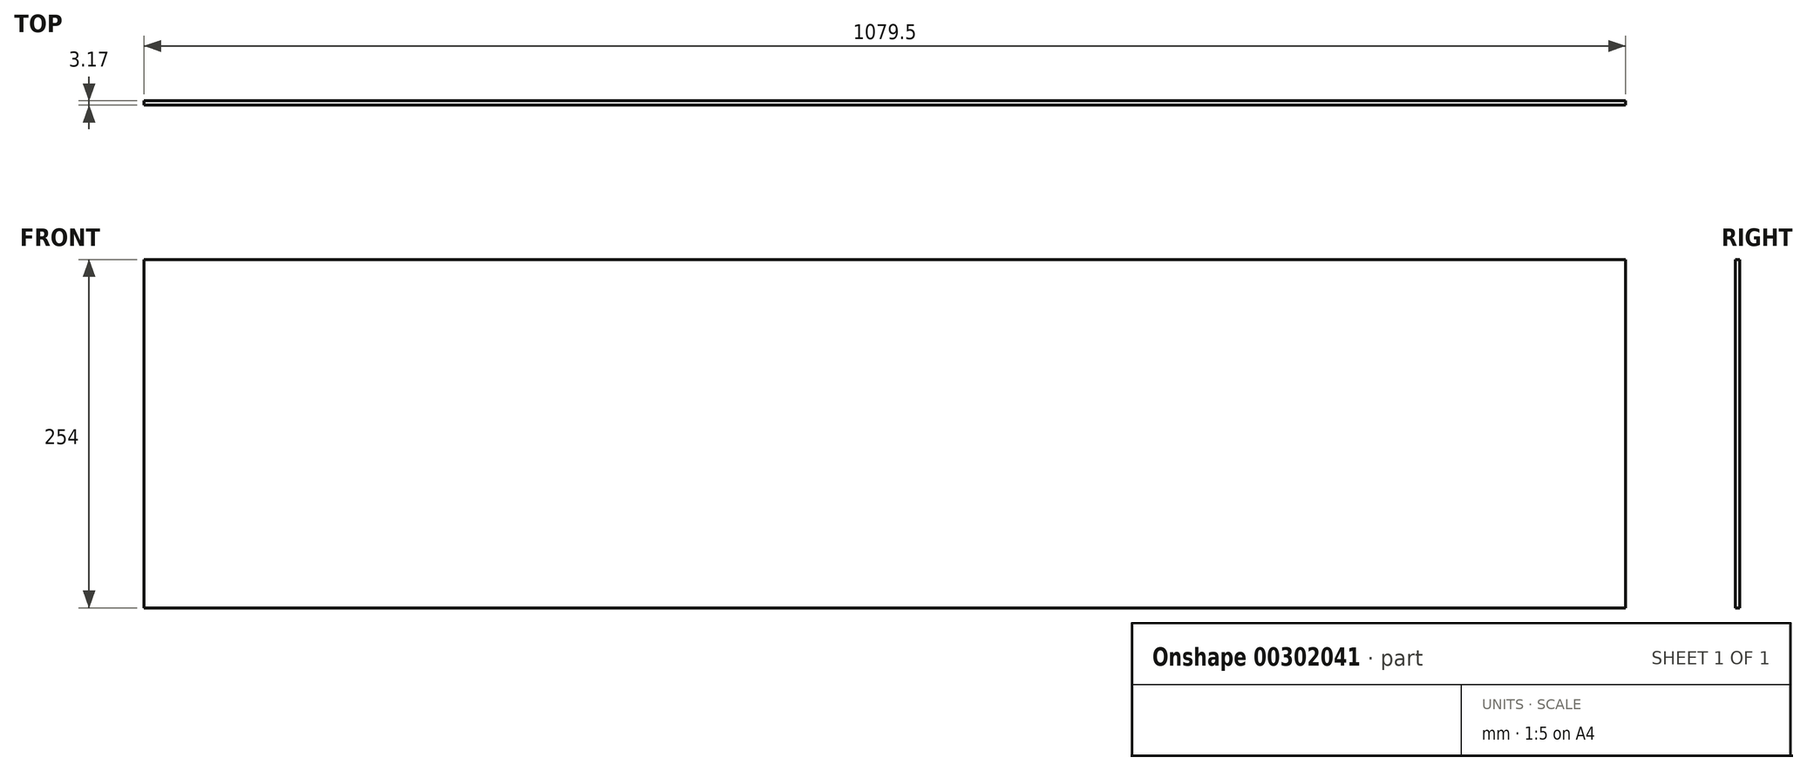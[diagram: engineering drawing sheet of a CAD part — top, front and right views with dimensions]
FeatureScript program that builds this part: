
annotation { "Feature Type Name" : "Feature", "Feature Type Description" : "" }
export const myFeature = defineFeature(function(context is Context, id is Id, definition is map)
    precondition{}
    {
        {
            var Q0;
            Q0=qCreatedBy(makeId("Front.planeOp"),FACE);
            var sketch = newSketch(context, id + "F0", { "sketchPlane" : qUnion([Q0])});
            skLineSegment(sketch, "E0.bottom", {"start": v(539.75, 127) * mm, "end": v(-539.75, 127) * mm});
            skLineSegment(sketch, "E0.top", {"start": v(539.75, -127) * mm, "end": v(-539.75, -127) * mm});
            skLineSegment(sketch, "E0.left", {"start": v(539.75, 127) * mm, "end": v(539.75, -127) * mm});
            skLineSegment(sketch, "E0.right", {"start": v(-539.75, 127) * mm, "end": v(-539.75, -127) * mm});
            skPoint(sketch, "E0.middle", {"position": v(0, 0) * mm});
            skSolve(sketch);
        }
        {
            var Q0;
            Q0=makeQuery(id+"F0.imprint","IMPRINT",FACE,{"disambiguationData":[TD([[makeQuery(id+"F0.imprint","IMPRINT",EDGE,{"derivedFrom":sQuery(id+"F0.wireOp",EDGE,"E0.bottom")}),1.0]])]});
            extrude(context, id + "F1", {"entities" : qUnion([Q0]), "depth" : 3.17 * mm});
        }
    });
